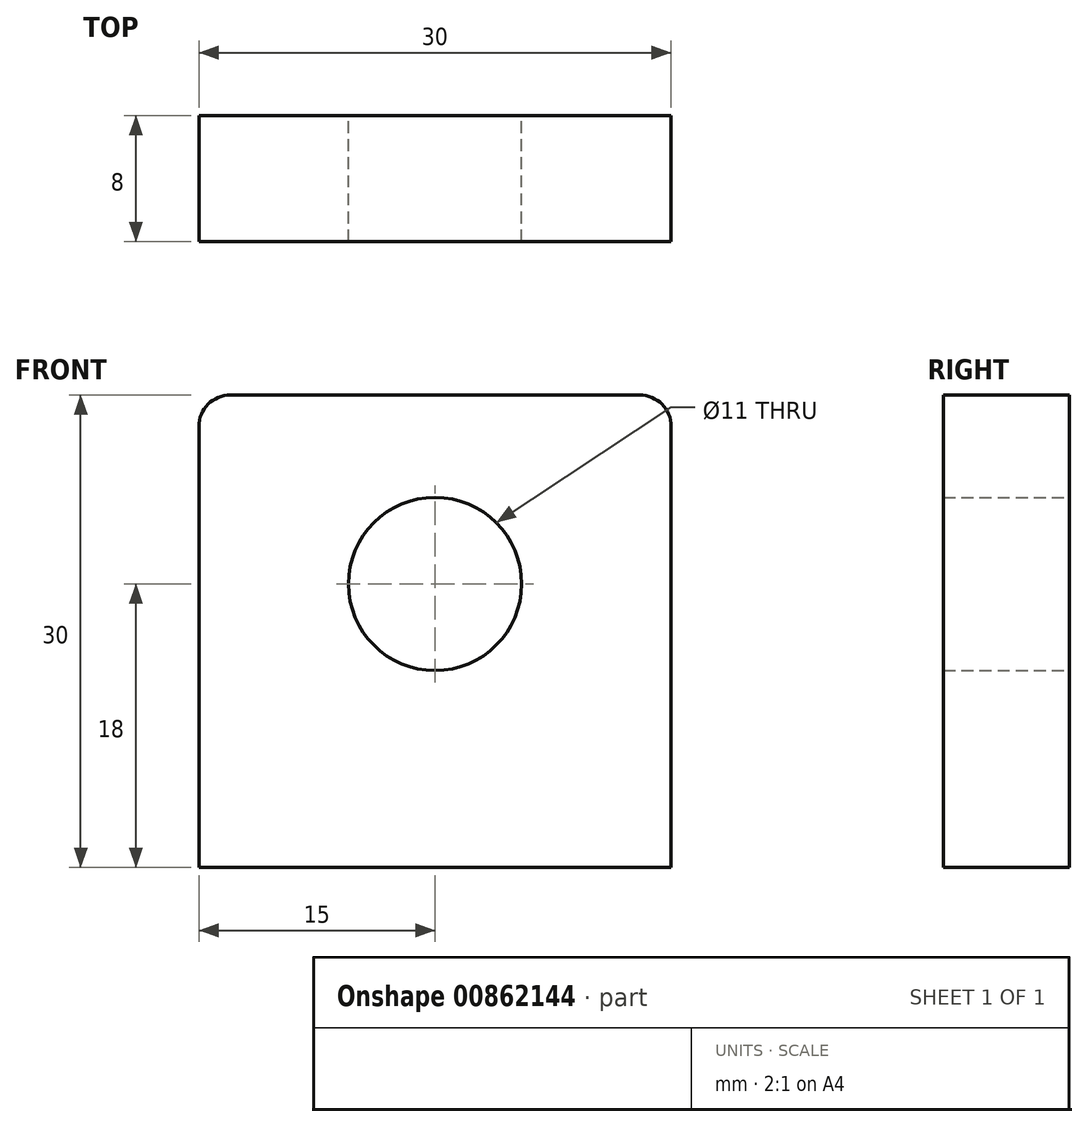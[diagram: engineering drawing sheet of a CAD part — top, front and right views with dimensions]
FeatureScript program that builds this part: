
annotation { "Feature Type Name" : "Feature", "Feature Type Description" : "" }
export const myFeature = defineFeature(function(context is Context, id is Id, definition is map)
    precondition{}
    {
        {
            var Q0;
            Q0=qCreatedBy(makeId("Front.planeOp"),FACE);
            var sketch = newSketch(context, id + "F0", { "sketchPlane" : qUnion([Q0])});
            skLineSegment(sketch, "E0.bottom", {"start": v(15, -15) * mm, "end": v(-15, -15) * mm});
            skLineSegment(sketch, "E0.top", {"start": v(13, 15) * mm, "end": v(-13, 15) * mm});
            skLineSegment(sketch, "E0.left", {"start": v(15, -15) * mm, "end": v(15, 13) * mm});
            skLineSegment(sketch, "E0.right", {"start": v(-15, -15) * mm, "end": v(-15, 13) * mm});
            skPoint(sketch, "E0.middle", {"position": v(0, 0) * mm});
            skPoint(sketch, "E1.visualSharp", {"position": v(-15, 15) * mm});
            skArc(sketch, "E1.filletArc", {"start": v(-13, 15) * mm, "mid": v(-14.41, 14.41) * mm, "end": v(-15, 13) * mm});
            skPoint(sketch, "E2.visualSharp", {"position": v(15, 15) * mm});
            skArc(sketch, "E2.filletArc", {"start": v(15, 13) * mm, "mid": v(14.41, 14.41) * mm, "end": v(13, 15) * mm});
            skCircle(sketch, "E3", {"center": v(0, 3) * mm, "radius": 5.5 * mm});
            skSolve(sketch);
        }
        {
            var Q0;
            Q0=makeQuery(id+"F0.imprint","IMPRINT",FACE,{"disambiguationData":[TD([[makeQuery(id+"F0.imprint","IMPRINT",EDGE,{"derivedFrom":sQuery(id+"F0.wireOp",EDGE,"E0.bottom")}),-1.0]])]});
            extrude(context, id + "F1", {"entities" : qUnion([Q0]), "depth" : 8 * mm, "offsetDistance" : 25 * mm});
        }
    });
